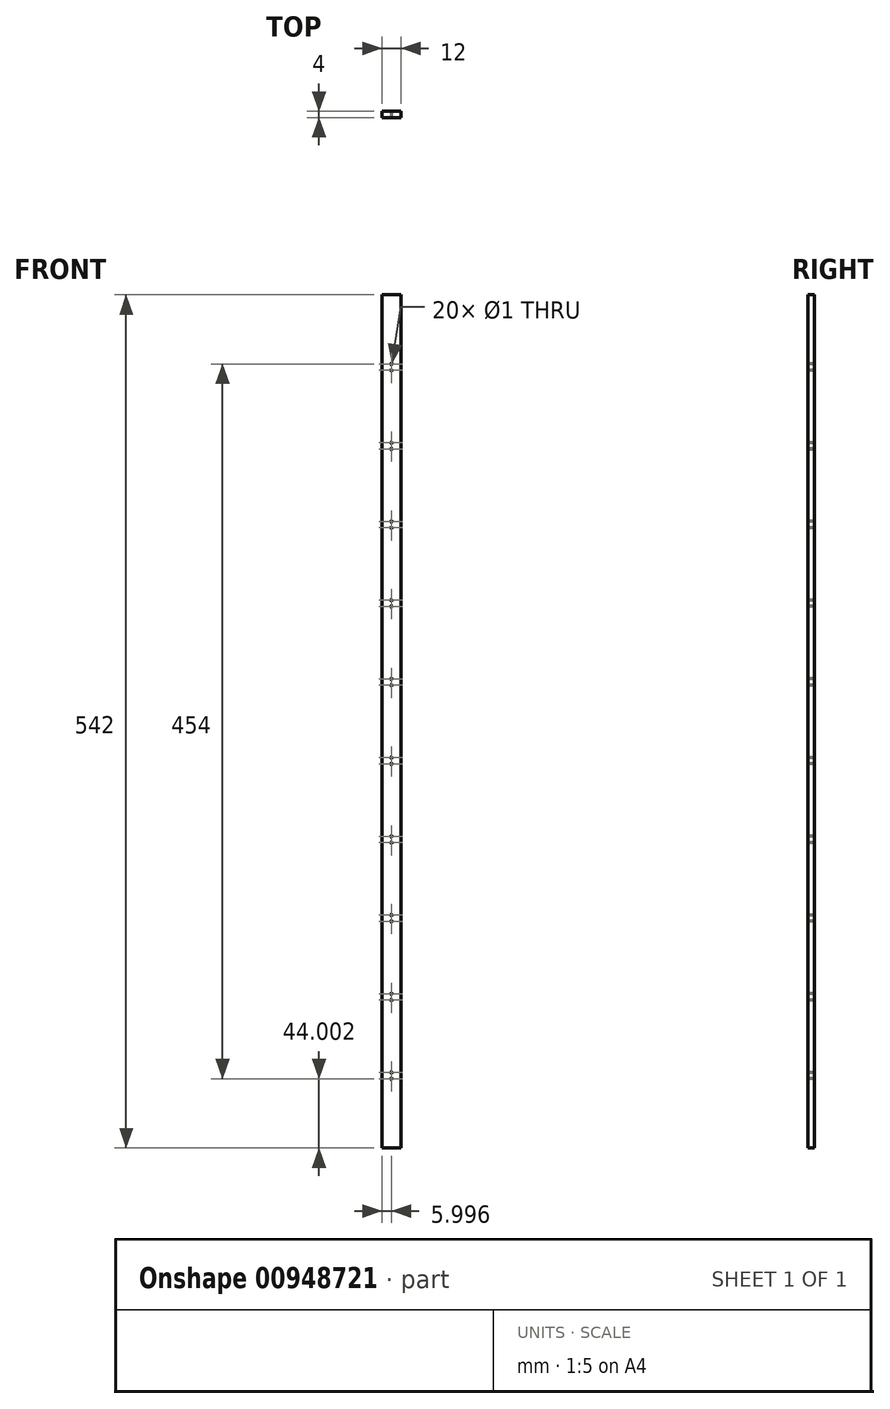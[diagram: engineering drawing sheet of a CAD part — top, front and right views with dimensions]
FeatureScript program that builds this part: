
annotation { "Feature Type Name" : "Feature", "Feature Type Description" : "" }
export const myFeature = defineFeature(function(context is Context, id is Id, definition is map)
    precondition{}
    {
        {
            var Q0;
            Q0=qCreatedBy(makeId("Front.planeOp"),FACE);
            var sketch = newSketch(context, id + "F0", { "sketchPlane" : qUnion([Q0])});
            skLineSegment(sketch, "E0.bottom", {"start": v(-34.56, 506.9) * mm, "end": v(-22.56, 506.9) * mm});
            skLineSegment(sketch, "E0.top", {"start": v(-34.56, -35.1) * mm, "end": v(-22.56, -35.1) * mm});
            skLineSegment(sketch, "E0.left", {"start": v(-34.56, 506.9) * mm, "end": v(-34.56, -35.1) * mm});
            skLineSegment(sketch, "E0.right", {"start": v(-22.56, 506.9) * mm, "end": v(-22.56, -35.1) * mm});
            skSolve(sketch);
        }
        {
            var Q0;
            Q0 = qSketchRegion(id + "F0", true);
            extrude(context, id + "F1", {"entities" : qUnion([Q0]), "depth" : 4 * mm, "offsetDistance" : 25 * mm});
        }
        {
            var Q0;
            Q0=makeQuery(id+"F1.opExtrude","CAP_FACE",FACE,{"disambiguationData":[OSD([sQuery(id+"F0.wireOp",EDGE,"E0.bottom"),sQuery(id+"F0.wireOp",EDGE,"E0.top"),sQuery(id+"F0.wireOp",EDGE,"E0.left"),sQuery(id+"F0.wireOp",EDGE,"E0.right")])],"isStart":false});
            var sketch = newSketch(context, id + "F2", { "sketchPlane" : qUnion([Q0])});
            skCircle(sketch, "E1", {"center": v(-28.56, 462.9) * mm, "radius": 0.5 * mm});
            skCircle(sketch, "E2", {"center": v(-28.56, 458.9) * mm, "radius": 0.5 * mm});
            skCircle(sketch, "E3.0.1.0", {"center": v(-28.56, 412.9) * mm, "radius": 0.5 * mm});
            skCircle(sketch, "E3.0.1.1", {"center": v(-28.56, 408.9) * mm, "radius": 0.5 * mm});
            skCircle(sketch, "E3.0.2.0", {"center": v(-28.56, 362.9) * mm, "radius": 0.5 * mm});
            skCircle(sketch, "E3.0.2.1", {"center": v(-28.56, 358.9) * mm, "radius": 0.5 * mm});
            skCircle(sketch, "E3.0.3.0", {"center": v(-28.56, 312.9) * mm, "radius": 0.5 * mm});
            skCircle(sketch, "E3.0.3.1", {"center": v(-28.56, 308.9) * mm, "radius": 0.5 * mm});
            skCircle(sketch, "E3.0.4.0", {"center": v(-28.56, 262.9) * mm, "radius": 0.5 * mm});
            skCircle(sketch, "E3.0.4.1", {"center": v(-28.56, 258.9) * mm, "radius": 0.5 * mm});
            skCircle(sketch, "E3.0.5.0", {"center": v(-28.56, 212.9) * mm, "radius": 0.5 * mm});
            skCircle(sketch, "E3.0.5.1", {"center": v(-28.56, 208.9) * mm, "radius": 0.5 * mm});
            skCircle(sketch, "E3.0.6.0", {"center": v(-28.56, 162.9) * mm, "radius": 0.5 * mm});
            skCircle(sketch, "E3.0.6.1", {"center": v(-28.56, 158.9) * mm, "radius": 0.5 * mm});
            skCircle(sketch, "E3.0.7.0", {"center": v(-28.56, 112.9) * mm, "radius": 0.5 * mm});
            skCircle(sketch, "E3.0.7.1", {"center": v(-28.56, 108.9) * mm, "radius": 0.5 * mm});
            skCircle(sketch, "E3.0.8.0", {"center": v(-28.56, 62.9) * mm, "radius": 0.5 * mm});
            skCircle(sketch, "E3.0.8.1", {"center": v(-28.56, 58.9) * mm, "radius": 0.5 * mm});
            skCircle(sketch, "E3.0.9.0", {"center": v(-28.56, 12.9) * mm, "radius": 0.5 * mm});
            skCircle(sketch, "E3.0.9.1", {"center": v(-28.56, 8.9) * mm, "radius": 0.5 * mm});
            skCircle(sketch, "E3.1.0.0", {"center": v(-3.56, 462.9) * mm, "radius": 0.5 * mm});
            skCircle(sketch, "E3.1.0.1", {"center": v(-3.56, 458.9) * mm, "radius": 0.5 * mm});
            skCircle(sketch, "E3.1.1.0", {"center": v(-3.56, 412.9) * mm, "radius": 0.5 * mm});
            skCircle(sketch, "E3.1.1.1", {"center": v(-3.56, 408.9) * mm, "radius": 0.5 * mm});
            skCircle(sketch, "E3.1.2.0", {"center": v(-3.56, 362.9) * mm, "radius": 0.5 * mm});
            skCircle(sketch, "E3.1.2.1", {"center": v(-3.56, 358.9) * mm, "radius": 0.5 * mm});
            skCircle(sketch, "E3.1.3.0", {"center": v(-3.56, 312.9) * mm, "radius": 0.5 * mm});
            skCircle(sketch, "E3.1.3.1", {"center": v(-3.56, 308.9) * mm, "radius": 0.5 * mm});
            skCircle(sketch, "E3.1.4.0", {"center": v(-3.56, 262.9) * mm, "radius": 0.5 * mm});
            skCircle(sketch, "E3.1.4.1", {"center": v(-3.56, 258.9) * mm, "radius": 0.5 * mm});
            skCircle(sketch, "E3.1.5.0", {"center": v(-3.56, 212.9) * mm, "radius": 0.5 * mm});
            skCircle(sketch, "E3.1.5.1", {"center": v(-3.56, 208.9) * mm, "radius": 0.5 * mm});
            skCircle(sketch, "E3.1.6.0", {"center": v(-3.56, 162.9) * mm, "radius": 0.5 * mm});
            skCircle(sketch, "E3.1.6.1", {"center": v(-3.56, 158.9) * mm, "radius": 0.5 * mm});
            skCircle(sketch, "E3.1.7.0", {"center": v(-3.56, 112.9) * mm, "radius": 0.5 * mm});
            skCircle(sketch, "E3.1.7.1", {"center": v(-3.56, 108.9) * mm, "radius": 0.5 * mm});
            skCircle(sketch, "E3.1.8.0", {"center": v(-3.56, 62.9) * mm, "radius": 0.5 * mm});
            skCircle(sketch, "E3.1.8.1", {"center": v(-3.56, 58.9) * mm, "radius": 0.5 * mm});
            skCircle(sketch, "E3.1.9.0", {"center": v(-3.56, 12.9) * mm, "radius": 0.5 * mm});
            skCircle(sketch, "E3.1.9.1", {"center": v(-3.56, 8.9) * mm, "radius": 0.5 * mm});
            skCircle(sketch, "E3.2.0.0", {"center": v(21.44, 462.9) * mm, "radius": 0.5 * mm});
            skCircle(sketch, "E3.2.0.1", {"center": v(21.44, 458.9) * mm, "radius": 0.5 * mm});
            skCircle(sketch, "E3.2.1.0", {"center": v(21.44, 412.9) * mm, "radius": 0.5 * mm});
            skCircle(sketch, "E3.2.1.1", {"center": v(21.44, 408.9) * mm, "radius": 0.5 * mm});
            skCircle(sketch, "E3.2.2.0", {"center": v(21.44, 362.9) * mm, "radius": 0.5 * mm});
            skCircle(sketch, "E3.2.2.1", {"center": v(21.44, 358.9) * mm, "radius": 0.5 * mm});
            skCircle(sketch, "E3.2.3.0", {"center": v(21.44, 312.9) * mm, "radius": 0.5 * mm});
            skCircle(sketch, "E3.2.3.1", {"center": v(21.44, 308.9) * mm, "radius": 0.5 * mm});
            skCircle(sketch, "E3.2.4.0", {"center": v(21.44, 262.9) * mm, "radius": 0.5 * mm});
            skCircle(sketch, "E3.2.4.1", {"center": v(21.44, 258.9) * mm, "radius": 0.5 * mm});
            skCircle(sketch, "E3.2.5.0", {"center": v(21.44, 212.9) * mm, "radius": 0.5 * mm});
            skCircle(sketch, "E3.2.5.1", {"center": v(21.44, 208.9) * mm, "radius": 0.5 * mm});
            skCircle(sketch, "E3.2.6.0", {"center": v(21.44, 162.9) * mm, "radius": 0.5 * mm});
            skCircle(sketch, "E3.2.6.1", {"center": v(21.44, 158.9) * mm, "radius": 0.5 * mm});
            skCircle(sketch, "E3.2.7.0", {"center": v(21.44, 112.9) * mm, "radius": 0.5 * mm});
            skCircle(sketch, "E3.2.7.1", {"center": v(21.44, 108.9) * mm, "radius": 0.5 * mm});
            skCircle(sketch, "E3.2.8.0", {"center": v(21.44, 62.9) * mm, "radius": 0.5 * mm});
            skCircle(sketch, "E3.2.8.1", {"center": v(21.44, 58.9) * mm, "radius": 0.5 * mm});
            skCircle(sketch, "E3.2.9.0", {"center": v(21.44, 12.9) * mm, "radius": 0.5 * mm});
            skCircle(sketch, "E3.2.9.1", {"center": v(21.44, 8.9) * mm, "radius": 0.5 * mm});
            skLineSegment(sketch, "E3.direction1", {"start": v(-28.56, 462.9) * mm, "end": v(-3.56, 462.9) * mm, "construction": true});
            skLineSegment(sketch, "E3.direction2", {"start": v(-28.56, 462.9) * mm, "end": v(-28.56, 412.9) * mm, "construction": true});
            skSolve(sketch);
        }
        {
            var Q0;
            Q0 = qSketchRegion(id + "F2", true);
            extrude(context, id + "F3", {"entities" : qUnion([Q0]), "operationType" : NewBodyOperationType.REMOVE, "oppositeDirection" : true, "depth" : 25 * mm, "offsetDistance" : 25 * mm});
        }
    });
